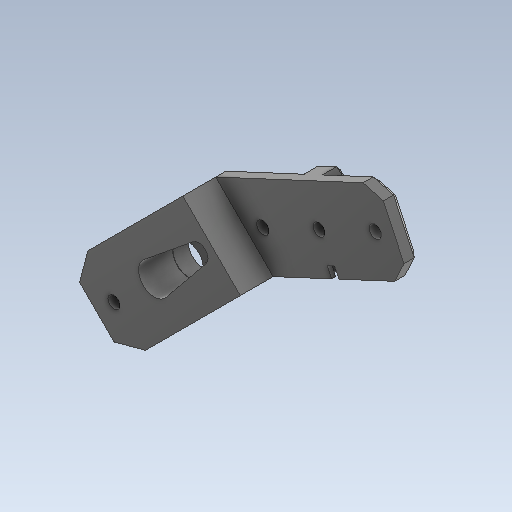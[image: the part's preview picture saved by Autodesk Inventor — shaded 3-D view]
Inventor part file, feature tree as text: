
AUTODESK INVENTOR PART (.ipt)
format: ipt  version: 2020 (Build 240168000, 168)  size: 391,680 bytes
history: native  units: in
note: dims shown in document units (in); Inventor stores cm internally (conversion verified against a paired STEP export)
features: sketch x12, other x6, extrude x6, projected_geometry x4, reference x1
ambient origin geometry x8: Origin, YZ Plane, XZ Plane, XY Plane, X Axis, Y Axis, Z Axis, Center Point
bodies: Solid1 (feature_tree)
feature tree (29):
  other  "TibiaTop.ipt"
  extrude  "Extrusion1"  Depth=0.3937in TaperAngle=0.0deg
  extrude  "Extrusion2"  Depth=0.1969in
  extrude  "Extrusion3"  Depth=0.0398in
  extrude  "Extrusion8"  Depth=0.1575in
  extrude  "Extrusion9"  Depth=0.4761in
  extrude  "Extrusion10"  Depth=0.0059in
  other  "Solid2::TibiaTop.ipt"
  other  "TaggingFeature1"
  sketch  "Sketch1"  dims[d0=0.3937in d1=0.3937in d2=0.0in]
  sketch  "Sketch9"  dims[d5=0.0398in d6=0.0398in]
  sketch  "Sketch10"  dims[d8=0.6142in d9=0.1575in]
  sketch  "Sketch11"  dims[d10=0.4761in d11=0.4761in]
  sketch  "Sketch15"  dims[d15=0.3307in d16=0.0in]
  sketch  "Sketch25"  dims[d34=0.0787in d35=0.0in]
  sketch  "Sketch26"  dims[d36=0.2756in d37=0.0787in d38=0.0in d39=0.0039in d40=0.3937in d41=0.0in d24=0.0197in d25=0.0344in d26=0.0197in d27=0.0344in d42=0.0197in d43=0.0344in]
  sketch  "Sketch8"  dims[d3=0.2835in d4=0.1969in]
  sketch  "Sketch12"  dims[d12=0.0059in d13=0.0059in]
  reference  "Reference1"
  sketch  "Sketch13"  dims[d14=0.0059in]
  projected_geometry  "Projected Loop1"
  projected_geometry  "Projected Loop6"
  sketch  "Sketch20"  dims[d17=0.3307in d18=0.0in]
  projected_geometry  "Projected Loop7"
  sketch  "Sketch21"  dims[d33=0.2756in]
  projected_geometry  "Projected Loop8"
  parser-record x1  (decoder bookkeeping rows leaked as tree rows — omitted from the tree; the rows remain in map.json)
  other  "LegDemoRight.iam"
  other  "TibiaTop:1"
note: 1 file-system path scrubbed to <path> (originals preserved in map.json)
